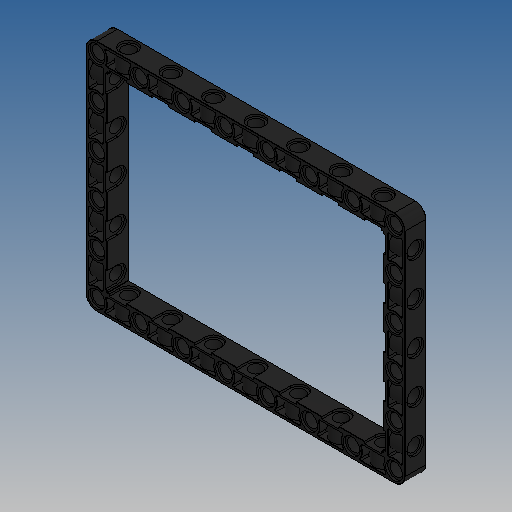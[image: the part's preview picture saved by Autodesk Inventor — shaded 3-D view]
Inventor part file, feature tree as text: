
AUTODESK INVENTOR PART (.ipt)
format: ipt  version: 2025 (Build 290162010, 162A)  size: 1,417,728 bytes
history: native  units: mm
features: sketch x13, extrude x11, pattern_linear x4, fillet x3, mirror x3, hole x2, projected_geometry x2
ambient origin geometry x8: Origin, YZ Plane, XZ Plane, XY Plane, X Axis, Y Axis, Z Axis, Center Point
bodies: Volumenkörper1 (feature_tree)
feature tree (38):
  extrude  "Extrusion1"  Depth=56.0mm
  fillet  "Rundung1"  Radius=40.0mm
  extrude  "Extrusion2"  Depth=8.0mm
  extrude  "Extrusion3"  Depth=4.0mm
  pattern_linear  "Rechteckige Anordnung1"  Count1=4 Spacing1=16.0mm
  pattern_linear  "Rechteckige Anordnung2"  Count1=3 Spacing1=16.0mm
  mirror  "Spiegeln1"
  extrude  "Extrusion4"  Depth=0.4mm
  extrude  "Extrusion8"  Depth=3.1mm TaperAngle=0.0deg
  fillet  "Rundung2"  Radius=0.1mm
  extrude  "Extrusion6"  Depth=7.2mm
  hole  "Bohrung1"  [1 undecoded]
  extrude  "Extrusion9"  Depth=16.0mm
  pattern_linear  "Rechteckige Anordnung3"  Spacing1=3.1mm  [1 undecoded]
  extrude  "Extrusion5"  TaperAngle=0.0deg  [1 undecoded]
  extrude  "Extrusion10"  Depth=0.8mm TaperAngle=0.0deg
  fillet  "Rundung3"  Radius=0.6mm
  extrude  "Extrusion11"  Depth=0.6mm
  hole  "Bohrung2"  [1 undecoded]
  extrude  "Extrusion12"  Depth=0.1mm
  pattern_linear  "Rechteckige Anordnung4"  Spacing1=7.2mm  [1 undecoded]
  mirror  "Spiegeln4"
  mirror  "Spiegeln5"
  sketch  "Skizze1"  dims[d0=4.0mm d1=56.0mm d2=40.0mm]
  sketch  "Skizze2"  dims[d3=0.1mm d4=8.0mm]
  sketch  "Skizze3"  dims[d5=8.0mm d6=4.0mm]
  sketch  "Skizze4"  dims[d7=0.0mm]
  sketch  "Skizze5"  dims[d8=6.4mm]
  sketch  "Skizze6"  dims[d9=0.8mm d10=0.0mm]
  sketch  "Skizze7"  dims[d11=4.8mm]
  sketch  "Skizze9"  dims[d12=0.8mm d13=0.0mm d14=40.0mm d16=16.0mm d17=30.0mm d19=16.0mm]
  projected_geometry  "Projizierte Kontur1"
  sketch  "Skizze10"  dims[d20=1.0mm d21=0.4mm]
  sketch  "Skizze11"  dims[d22=3.1mm d23=0.0mm d25=3.1mm d26=0.0mm d27=0.1mm]
  projected_geometry  "Projizierte Kontur2"
  sketch  "Skizze12"  dims[d28=0.1mm d29=7.2mm]
  sketch  "Skizze13"  dims[d30=10.0mm d31=0.0mm]
  sketch  "Skizze14"  dims[d32=4.8mm d33=6.0mm d34=6.4mm d35=0.8mm d36=90.0deg d37=8.0mm d38=20.594885mm d42=40.0mm d44=16.0mm d45=3.1mm d46=0.0mm d50=0.8mm d51=0.0mm d52=0.6mm d53=0.6mm d54=3.1mm d55=0.0mm d56=0.1mm d57=7.2mm d58=3.1mm d59=0.0mm d60=4.8mm d61=6.0mm d62=6.4mm d63=0.8mm d64=90.0deg d65=8.0mm d66=20.594885mm d67=0.8mm d68=0.0mm d69=30.0mm d71=16.0mm]
note: 5 required parameter values undecoded (feature->parameter linkage not recoverable at this tier; creation-order binding heuristic only, values carry confidence <= 0.55)
